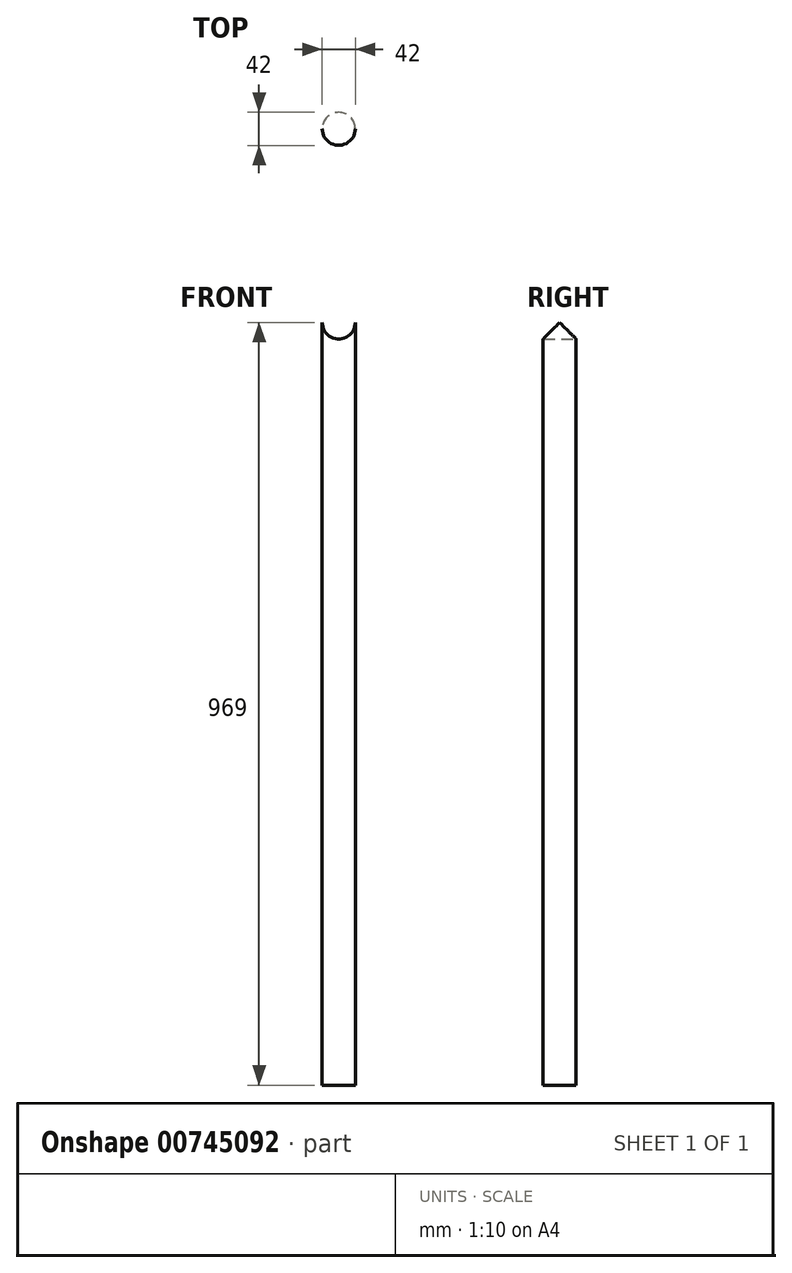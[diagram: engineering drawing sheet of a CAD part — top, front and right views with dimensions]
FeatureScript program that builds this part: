
annotation { "Feature Type Name" : "Feature", "Feature Type Description" : "" }
export const myFeature = defineFeature(function(context is Context, id is Id, definition is map)
    precondition{}
    {
        {
            var Q0;
            Q0=qCreatedBy(makeId("Top.planeOp"),FACE);
            var sketch = newSketch(context, id + "F0", { "sketchPlane" : qUnion([Q0])});
            skCircle(sketch, "E0", {"center": v(0, 0) * mm, "radius": 21 * mm});
            skSolve(sketch);
        }
        {
            var Q0;
            Q0=makeQuery(id+"F0.imprint","IMPRINT",FACE,{"disambiguationData":[TD([[makeQuery(id+"F0.imprint","IMPRINT",EDGE,{"derivedFrom":sQuery(id+"F0.wireOp",EDGE,"E0")}),1.0]])]});
            extrude(context, id + "F1", {"entities" : qUnion([Q0]), "oppositeDirection" : true, "depth" : (990 - 21) * mm, "offsetDistance" : 25 * mm});
        }
        {
            var Q0;
            Q0=qCreatedBy(makeId("Front.planeOp"),FACE);
            var sketch = newSketch(context, id + "F2", { "sketchPlane" : qUnion([Q0])});
            skCircle(sketch, "E1", {"center": v(0, 0) * mm, "radius": 21 * mm});
            skSolve(sketch);
        }
        {
            var Q0;
            Q0=makeQuery(id+"F2.imprint","IMPRINT",FACE,{"disambiguationData":[TD([[makeQuery(id+"F2.imprint","IMPRINT",EDGE,{"derivedFrom":sQuery(id+"F2.wireOp",EDGE,"E1")}),1.0]])]});
            extrude(context, id + "F3", {"entities" : qUnion([Q0]), "operationType" : NewBodyOperationType.REMOVE, "endBound" : BoundingType.SYMMETRIC, "depth" : 100 * mm, "offsetDistance" : 25 * mm});
        }
    });
